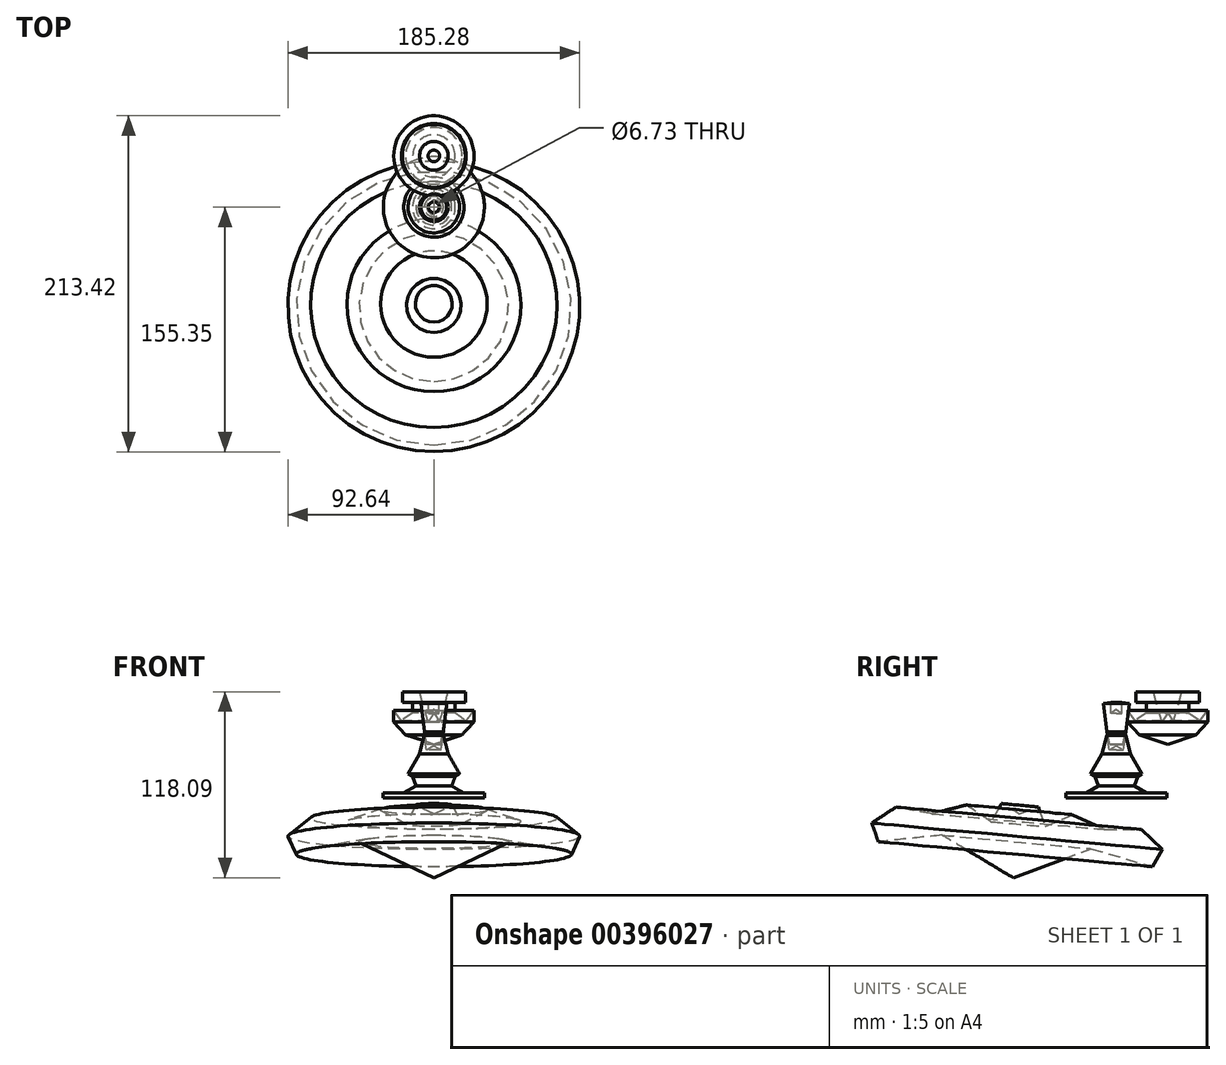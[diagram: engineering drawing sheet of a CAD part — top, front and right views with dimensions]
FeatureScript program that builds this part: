
annotation { "Feature Type Name" : "Feature", "Feature Type Description" : "" }
export const myFeature = defineFeature(function(context is Context, id is Id, definition is map)
    precondition{}
    {
        {
            var Q0;
            Q0=qCreatedBy(makeId("Front.planeOp"),FACE);
            var sketch = newSketch(context, id + "F0", { "sketchPlane" : qUnion([Q0])});
            skLineSegment(sketch, "E0", {"start": v(6.12, 39.66) * mm, "end": v(9.06, 28.06) * mm});
            skLineSegment(sketch, "E1", {"start": v(9.06, 28.06) * mm, "end": v(16.33, 15.22) * mm});
            skLineSegment(sketch, "E2", {"start": v(16.33, 15.22) * mm, "end": v(13.6, 13.68) * mm});
            skLineSegment(sketch, "E3", {"start": v(13.6, 13.68) * mm, "end": v(11.38, 7.5) * mm});
            skLineSegment(sketch, "E4", {"start": v(11.38, 7.5) * mm, "end": v(19.1, 3) * mm});
            skLineSegment(sketch, "E5", {"start": v(19.1, 3) * mm, "end": v(32.1, 3) * mm});
            skLineSegment(sketch, "E6", {"start": v(32.1, 3) * mm, "end": v(32.1, 0) * mm});
            skLineSegment(sketch, "E7", {"start": v(32.1, 0) * mm, "end": v(0, 0) * mm});
            skLineSegment(sketch, "E8", {"start": v(6.12, 39.66) * mm, "end": v(4.5, 30.48) * mm});
            skLineSegment(sketch, "E9", {"start": v(4.5, 30.48) * mm, "end": v(0, 33) * mm});
            skLineSegment(sketch, "E10", {"start": v(0, 33) * mm, "end": v(0, 0) * mm});
            skSolve(sketch);
        }
        {
            var Q0;
            Q0 = qSketchRegion(id + "F0", true);
            var Q1;
            Q1=sQuery(id+"F0.wireOp",EDGE,"E10");
            revolve(context, id + "F1", {"entities" : qUnion([Q0]), "axis" : qUnion([Q1]), "revolveType" : RevolveType.FULL});
        }
        {
            var Q0;
            Q0=qCreatedBy(makeId("Front.planeOp"),FACE);
            var sketch = newSketch(context, id + "F2", { "sketchPlane" : qUnion([Q0])});
            skLineSegment(sketch, "E11", {"start": v(0, 56.2) * mm, "end": v(0, 33.89) * mm});
            skLineSegment(sketch, "E12", {"start": v(0, 33.89) * mm, "end": v(4.19, 34.07) * mm});
            skLineSegment(sketch, "E13", {"start": v(4.19, 34.07) * mm, "end": v(6.02, 41.76) * mm});
            skLineSegment(sketch, "E14", {"start": v(6.02, 41.76) * mm, "end": v(8.2, 59.91) * mm});
            skLineSegment(sketch, "E15", {"start": v(8.2, 59.91) * mm, "end": v(3.37, 60.5) * mm});
            skLineSegment(sketch, "E16", {"start": v(3.37, 60.5) * mm, "end": v(3.37, 53.57) * mm});
            skLineSegment(sketch, "E17", {"start": v(3.37, 53.57) * mm, "end": v(0, 56.2) * mm});
            skSolve(sketch);
        }
        {
            var Q0;
            Q0 = qSketchRegion(id + "F2", true);
            var Q1;
            Q1=sQuery(id+"F2.wireOp",EDGE,"E11");
            revolve(context, id + "F3", {"entities" : qUnion([Q0]), "axis" : qUnion([Q1]), "revolveType" : RevolveType.FULL});
        }
        {
            var Q0;
            Q0=qCreatedBy(makeId("Right.planeOp"),FACE);
            var sketch = newSketch(context, id + "F4", { "sketchPlane" : qUnion([Q0])});
            skLineSegment(sketch, "E18", {"start": v(32.58, 53.81) * mm, "end": v(32.58, 34.05) * mm});
            skLineSegment(sketch, "E19", {"start": v(32.58, 34.05) * mm, "end": v(50.53, 40.03) * mm});
            skLineSegment(sketch, "E20", {"start": v(50.53, 40.03) * mm, "end": v(58.07, 48.35) * mm});
            skLineSegment(sketch, "E21", {"start": v(58.07, 48.35) * mm, "end": v(58.07, 55.63) * mm});
            skLineSegment(sketch, "E22", {"start": v(58.07, 55.63) * mm, "end": v(53.13, 48.87) * mm});
            skLineSegment(sketch, "E23", {"start": v(53.13, 48.87) * mm, "end": v(46, 54.08) * mm});
            skLineSegment(sketch, "E24", {"start": v(46, 54.08) * mm, "end": v(46, 60.57) * mm});
            skLineSegment(sketch, "E25", {"start": v(46, 60.57) * mm, "end": v(52.6, 60.57) * mm});
            skLineSegment(sketch, "E26", {"start": v(52.6, 60.57) * mm, "end": v(52.6, 67.33) * mm});
            skLineSegment(sketch, "E27", {"start": v(52.6, 67.33) * mm, "end": v(41.68, 67.33) * mm});
            skLineSegment(sketch, "E28", {"start": v(41.68, 67.33) * mm, "end": v(36.22, 48.1) * mm});
            skLineSegment(sketch, "E29", {"start": v(36.22, 48.1) * mm, "end": v(32.58, 53.81) * mm});
            skSolve(sketch);
        }
        {
            var Q0;
            Q0 = qSketchRegion(id + "F4", true);
            var Q1;
            Q1=sQuery(id+"F4.wireOp",EDGE,"E18");
            revolve(context, id + "F5", {"entities" : qUnion([Q0]), "axis" : qUnion([Q1]), "revolveType" : RevolveType.FULL});
        }
        {
            var Q0;
            Q0=qCreatedBy(makeId("Right.planeOp"),FACE);
            var sketch = newSketch(context, id + "F6", { "sketchPlane" : qUnion([Q0])});
            skLineSegment(sketch, "E30", {"start": v(-45.2, -18.25) * mm, "end": v(-49.63, -5.77) * mm});
            skLineSegment(sketch, "E31", {"start": v(-49.63, -5.77) * mm, "end": v(-61.78, -10.08) * mm});
            skLineSegment(sketch, "E32", {"start": v(-61.78, -10.08) * mm, "end": v(-65.5, -50.76) * mm});
            skLineSegment(sketch, "E33", {"start": v(-65.5, -50.76) * mm, "end": v(-16.08, -32.3) * mm});
            skLineSegment(sketch, "E34", {"start": v(-16.08, -32.3) * mm, "end": v(22.93, -43.74) * mm});
            skLineSegment(sketch, "E35", {"start": v(22.93, -43.74) * mm, "end": v(29.17, -32.82) * mm});
            skLineSegment(sketch, "E36", {"start": v(29.17, -32.82) * mm, "end": v(15.9, -20.07) * mm});
            skLineSegment(sketch, "E37", {"start": v(15.9, -20.07) * mm, "end": v(-7.24, -20.07) * mm});
            skLineSegment(sketch, "E38", {"start": v(-7.24, -20.07) * mm, "end": v(-27.78, -10.71) * mm});
            skLineSegment(sketch, "E39", {"start": v(-27.78, -10.71) * mm, "end": v(-45.2, -18.25) * mm});
            skSolve(sketch);
        }
        {
            var Q0;
            Q0 = qSketchRegion(id + "F6", true);
            var Q1;
            Q1=sQuery(id+"F6.wireOp",EDGE,"E32");
            revolve(context, id + "F7", {"entities" : qUnion([Q0]), "axis" : qUnion([Q1]), "revolveType" : RevolveType.FULL});
        }
    });
